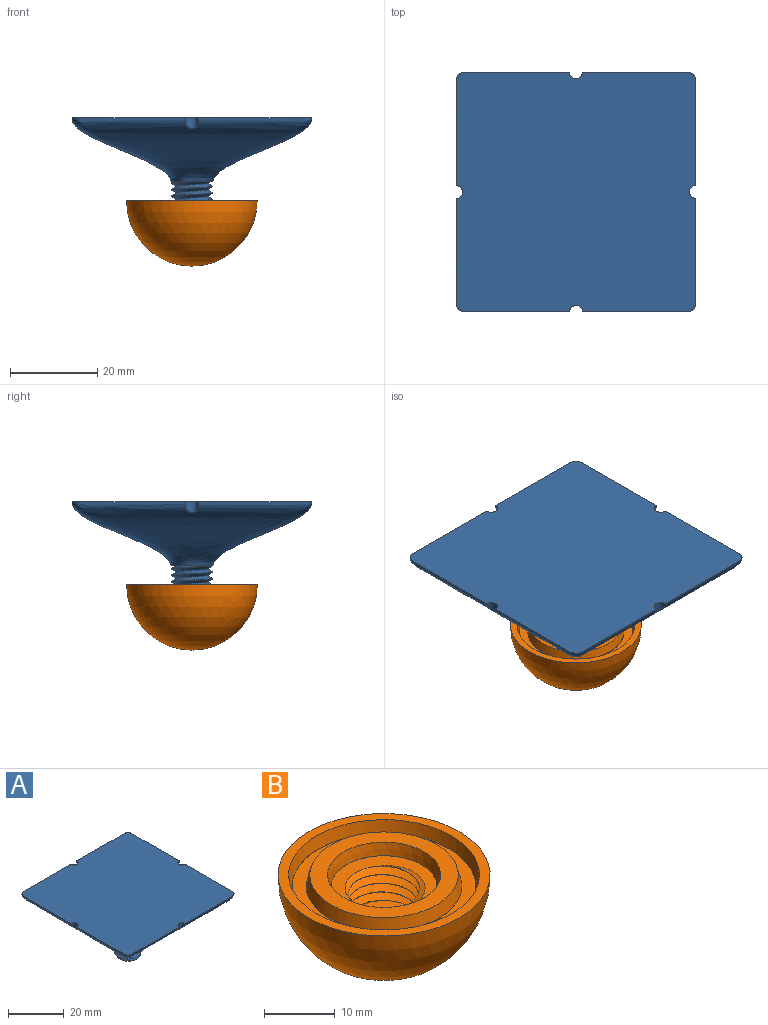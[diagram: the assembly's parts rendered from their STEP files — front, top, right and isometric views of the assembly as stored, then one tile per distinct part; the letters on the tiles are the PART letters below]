
ASSEMBLY  parts=2 mates=1
PART A: 14 faces, bbox 55x55x27.8 mm
  f0: cylinder r=4.75mm len=11mm, axis (0,0,1), area 21mm2, adj f2,f4,f5,f6,f7
  f1: plane 7.53x7.39mm, normal (0,0,-1), area 43.8mm2, adj f2,f6,f7
  f2: cone r=4.75mm half-angle=45deg, axis (0,0,1), area 16.5mm2, adj f0,f1,f6,f7
  f3: plane 55x55mm, normal (0,0,1), area 3007.4mm2, adj f4,f10,f11,f12,f13
  f4: bspline ~55x55mm, area 3561.5mm2, adj f0,f3,f5,f6,f7,f9,f10,f11
  f5: bspline ~28.64x23.09mm, area 0.1mm2, adj f0,f4,f6
  f6: bspline ~14.3x9.78mm, area 310.7mm2, adj f0,f1,f2,f4,f5,f7,f8,f9
  f7: bspline ~14.45x9.78mm, area 328.9mm2, adj f0,f1,f2,f4,f6,f8,f9
  f8: plane 1.44x1.25mm, normal (0,-1,0), area 0.9mm2, adj f6,f7,f9
  f9: bspline ~9.65x9.57mm, area 33.5mm2, adj f4,f6,f7,f8
  f10: cylinder r=1.5mm len=3mm, axis (0,0,1), area 8.8mm2, adj f3,f4
  f11: cylinder r=1.5mm len=3mm, axis (0,0,1), area 8.8mm2, adj f3,f4
  f12: cylinder r=1.5mm len=3mm, axis (0,0,1), area 8.8mm2, adj f3,f4
  f13: cylinder r=1.5mm len=3mm, axis (0,0,1), area 8.8mm2, adj f3,f4
PART B: 17 faces, bbox 31.1x31.1x16.1 mm
  f0: cylinder r=5mm len=10mm, axis (0,0,1), area 10.5mm2, adj f8,f9,f11,f12,f13
  f1: plane 30x30mm, normal (0,0,1), area 134.3mm2, adj f2,f14
  f2: sphere r=15mm, area 1413.7mm2, adj f1
  f3: cylinder r=11mm len=22mm, axis (0,0,1), area 0.7mm2, adj f5,f15
  f4: cylinder r=13mm len=26mm, axis (0,0,1), area 0.8mm2, adj f5,f14
  f5: plane 26x26mm, normal (0,0,1), area 150.8mm2, adj f3,f4
  f6: plane 21x21mm, normal (0,0,1), area 145.3mm2, adj f15,f16
  f7: cylinder r=7.5mm len=15mm, axis (0,0,1), area 0.5mm2, adj f8,f16
  f8: plane 16.13x16.13mm, normal (0,0,1), area 76.8mm2, adj f0,f7,f12,f13
  f9: plane 10x10mm, normal (0,0,1), area 78.5mm2, adj f0,f10
  f10: cylinder r=5mm len=10mm, axis (0,0,-1), area 9.2mm2, adj f9,f11,f12
  f11: plane 1.45x1.3mm, normal (0,-1,0), area 0.9mm2, adj f0,f10,f12,f13
  f12: bspline ~14.54x12.59mm, area 225.4mm2, adj f0,f8,f10,f11,f13
  f13: bspline ~14.54x12.59mm, area 215.7mm2, adj f0,f8,f11,f12
  f14: cone r=13mm half-angle=14.1deg, axis (0,0,1), area 170.8mm2, adj f1,f4
  f15: cone r=10.5mm half-angle=14.1deg, axis (0,0,-1), area 138.6mm2, adj f3,f6
  f16: cone r=7.5mm half-angle=14.1deg, axis (0,0,1), area 99.9mm2, adj f6,f7
PLACE A t=(-6.55,-1.74,8.12)mm fixed
PLACE B rot(axis=(0,0,-1),137.5deg) t=(-6.59,-1.73,4.12)mm
MATE cylindrical A.f1 <-> B.f0  axis (0,0,-1) through (-6.59,-1.73,-3.88)mm
